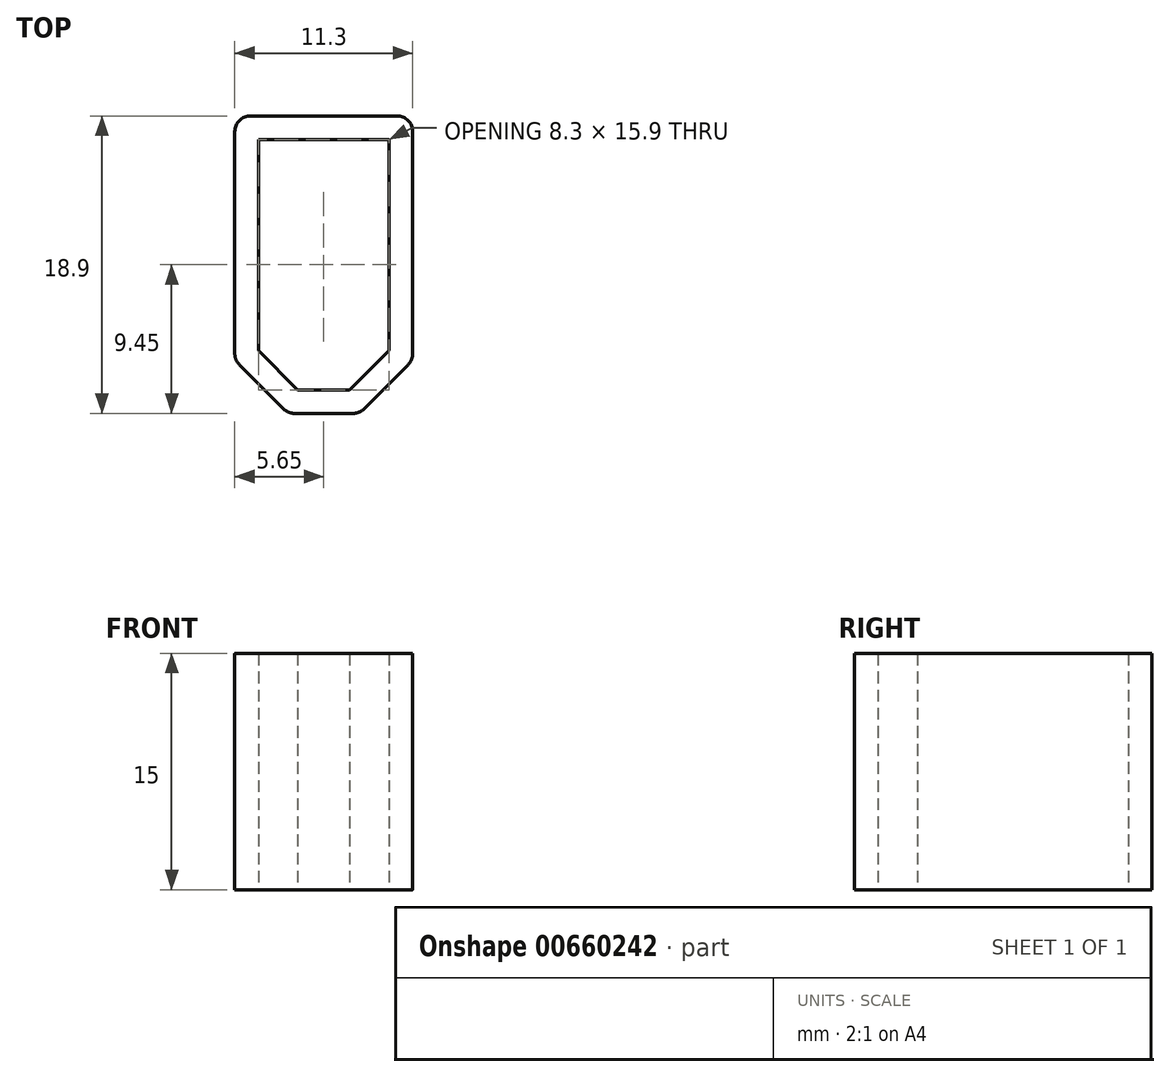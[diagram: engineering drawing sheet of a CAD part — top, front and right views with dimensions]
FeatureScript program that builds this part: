
annotation { "Feature Type Name" : "Feature", "Feature Type Description" : "" }
export const myFeature = defineFeature(function(context is Context, id is Id, definition is map)
    precondition{}
    {
        {
            var Q0;
            Q0=qCreatedBy(makeId("Top.planeOp"),FACE);
            var sketch = newSketch(context, id + "F0", { "sketchPlane" : qUnion([Q0])});
            skLineSegment(sketch, "E0.bottom", {"start": v(4.15, 8) * mm, "end": v(-4.15, 8) * mm});
            skLineSegment(sketch, "E0.top", {"start": v(1.65, -7.9) * mm, "end": v(-1.65, -7.9) * mm});
            skLineSegment(sketch, "E0.left", {"start": v(4.15, 8) * mm, "end": v(4.15, -5.4) * mm});
            skLineSegment(sketch, "E0.right", {"start": v(-4.15, 8) * mm, "end": v(-4.15, -5.4) * mm});
            skPoint(sketch, "E0.middle", {"position": v(0, 0) * mm});
            skLineSegment(sketch, "E1", {"start": v(1.65, -7.9) * mm, "end": v(4.15, -5.4) * mm});
            skLineSegment(sketch, "E2.MirrorCS", {"start": v(-1.65, -7.9) * mm, "end": v(-4.15, -5.4) * mm});
            skLineSegment(sketch, "E3.0", {"start": v(5.65, 9.5) * mm, "end": v(5.65, -6.02) * mm});
            skLineSegment(sketch, "E3.1", {"start": v(-5.65, 9.5) * mm, "end": v(-5.65, -6.02) * mm});
            skLineSegment(sketch, "E3.2", {"start": v(-2.27, -9.4) * mm, "end": v(-5.65, -6.02) * mm});
            skLineSegment(sketch, "E3.3", {"start": v(5.65, 9.5) * mm, "end": v(-5.65, 9.5) * mm});
            skLineSegment(sketch, "E3.4", {"start": v(2.27, -9.4) * mm, "end": v(-2.27, -9.4) * mm});
            skLineSegment(sketch, "E3.5", {"start": v(2.27, -9.4) * mm, "end": v(5.65, -6.02) * mm});
            skSolve(sketch);
        }
        {
            var Q0;
            Q0=makeQuery(id+"F0.imprint","IMPRINT",FACE,{"disambiguationData":[TD([[makeQuery(id+"F0.imprint","IMPRINT",EDGE,{"derivedFrom":sQuery(id+"F0.wireOp",EDGE,"E0.bottom")}),-1.0]])]});
            extrude(context, id + "F1", {"entities" : qUnion([Q0]), "depth" : 15 * mm, "offsetDistance" : 25 * mm});
        }
        {
            var Q0;
            Q0=makeQuery(id+"F1.opExtrude","SWEPT_EDGE",EDGE,{"disambiguationData":[OSD([sQuery(id+"F0.wireOp",EDGE,"E3.1"),sQuery(id+"F0.wireOp",EDGE,"E3.3")])]});
            var Q1;
            Q1=makeQuery(id+"F1.opExtrude","SWEPT_EDGE",EDGE,{"disambiguationData":[OSD([sQuery(id+"F0.wireOp",EDGE,"E3.0"),sQuery(id+"F0.wireOp",EDGE,"E3.3")])]});
            var Q2;
            Q2=makeQuery(id+"F1.opExtrude","SWEPT_EDGE",EDGE,{"disambiguationData":[OSD([sQuery(id+"F0.wireOp",EDGE,"E3.0"),sQuery(id+"F0.wireOp",EDGE,"E3.5")])]});
            var Q3;
            Q3=makeQuery(id+"F1.opExtrude","SWEPT_EDGE",EDGE,{"disambiguationData":[OSD([sQuery(id+"F0.wireOp",EDGE,"E3.4"),sQuery(id+"F0.wireOp",EDGE,"E3.5")])]});
            var Q4;
            Q4=makeQuery(id+"F1.opExtrude","SWEPT_EDGE",EDGE,{"disambiguationData":[OSD([sQuery(id+"F0.wireOp",EDGE,"E3.2"),sQuery(id+"F0.wireOp",EDGE,"E3.4")])]});
            var Q5;
            Q5=makeQuery(id+"F1.opExtrude","SWEPT_EDGE",EDGE,{"disambiguationData":[OSD([sQuery(id+"F0.wireOp",EDGE,"E3.1"),sQuery(id+"F0.wireOp",EDGE,"E3.2")])]});
            fillet(context, id + "F2", {"entities" : qUnion([Q0, Q1, Q2, Q3, Q4, Q5]), "radius" : 1 * mm, "tangentPropagation" : true, "allowEdgeOverflow" : false});
        }
    });
